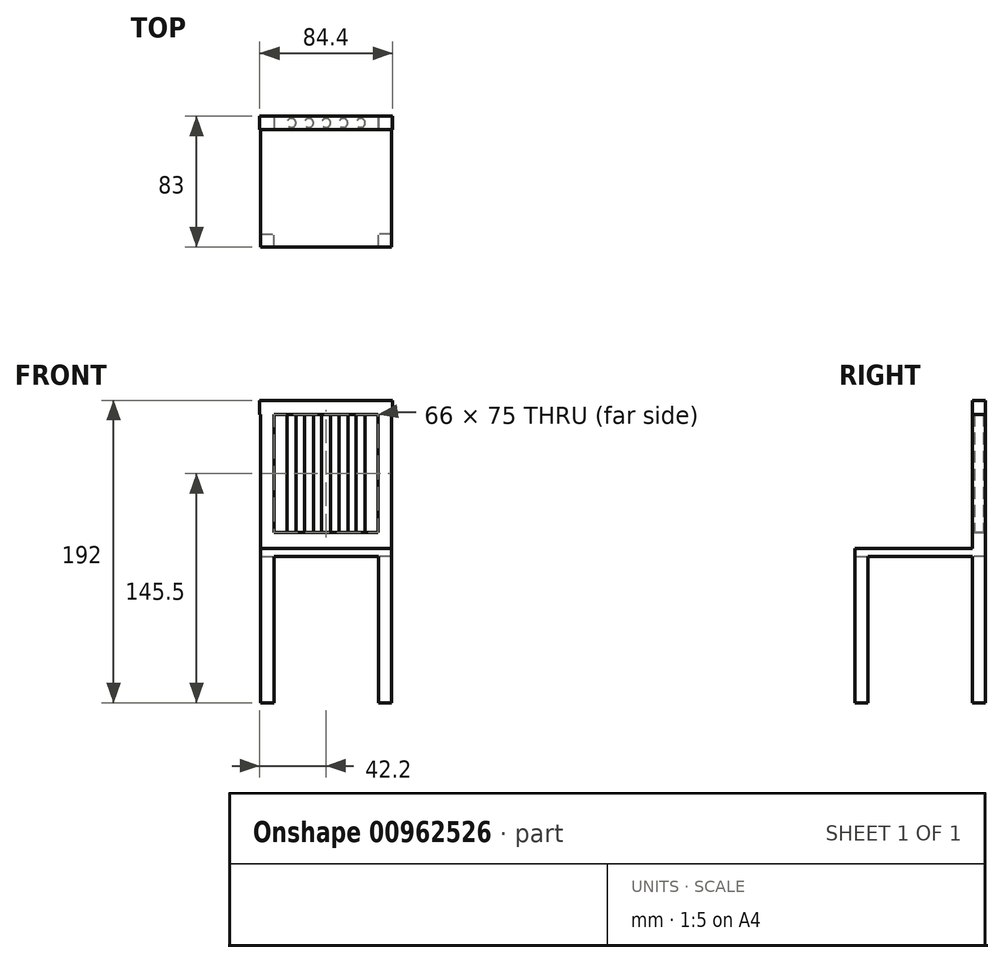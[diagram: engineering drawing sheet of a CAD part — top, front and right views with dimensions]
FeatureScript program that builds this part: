
annotation { "Feature Type Name" : "Feature", "Feature Type Description" : "" }
export const myFeature = defineFeature(function(context is Context, id is Id, definition is map)
    precondition{}
    {
        {
            var Q0;
            Q0=qCreatedBy(makeId("Top.planeOp"),FACE);
            var sketch = newSketch(context, id + "F0", { "sketchPlane" : qUnion([Q0])});
            skLineSegment(sketch, "E0.bottom", {"start": v(41.5, -41.5) * mm, "end": v(-41.5, -41.5) * mm});
            skLineSegment(sketch, "E0.top", {"start": v(41.5, 41.5) * mm, "end": v(-41.5, 41.5) * mm});
            skLineSegment(sketch, "E0.left", {"start": v(41.5, -41.5) * mm, "end": v(41.5, 41.5) * mm});
            skLineSegment(sketch, "E0.right", {"start": v(-41.5, -41.5) * mm, "end": v(-41.5, 41.5) * mm});
            skPoint(sketch, "E0.middle", {"position": v(0, 0) * mm});
            skSolve(sketch);
        }
        {
            var Q0;
            Q0 = qSketchRegion(id + "F0", true);
            extrude(context, id + "F1", {"entities" : qUnion([Q0]), "depth" : 5 * mm, "offsetDistance" : 25 * mm});
        }
        {
            var Q0;
            Q0=makeQuery(id+"F1.opExtrude","CAP_FACE",FACE,{"disambiguationData":[OSD([sQuery(id+"F0.wireOp",EDGE,"E0.bottom"),sQuery(id+"F0.wireOp",EDGE,"E0.top"),sQuery(id+"F0.wireOp",EDGE,"E0.left"),sQuery(id+"F0.wireOp",EDGE,"E0.right")])],"isStart":false});
            var sketch = newSketch(context, id + "F2", { "sketchPlane" : qUnion([Q0])});
            skLineSegment(sketch, "E1.bottom", {"start": v(-41.5, 41.5) * mm, "end": v(41.5, 41.5) * mm});
            skLineSegment(sketch, "E1.top", {"start": v(-41.5, 33) * mm, "end": v(41.5, 33) * mm});
            skLineSegment(sketch, "E1.left", {"start": v(-41.5, 41.5) * mm, "end": v(-41.5, 33) * mm});
            skLineSegment(sketch, "E1.right", {"start": v(41.5, 41.5) * mm, "end": v(41.5, 33) * mm});
            skSolve(sketch);
        }
        {
            var Q0;
            Q0 = qSketchRegion(id + "F2", true);
            extrude(context, id + "F3", {"entities" : qUnion([Q0]), "operationType" : NewBodyOperationType.ADD, "depth" : 10 * mm, "offsetDistance" : 25 * mm});
        }
        {
            var Q0;
            Q0=makeQuery(id+"F3.opExtrude","CAP_FACE",FACE,{"disambiguationData":[OSD([sQuery(id+"F2.wireOp",EDGE,"E1.bottom"),sQuery(id+"F2.wireOp",EDGE,"E1.top"),sQuery(id+"F2.wireOp",EDGE,"E1.left"),sQuery(id+"F2.wireOp",EDGE,"E1.right")])],"isStart":false});
            var sketch = newSketch(context, id + "F4", { "sketchPlane" : qUnion([Q0])});
            skLineSegment(sketch, "E2.bottom", {"start": v(-41.5, 41.5) * mm, "end": v(-33, 41.5) * mm});
            skLineSegment(sketch, "E2.top", {"start": v(-41.5, 33) * mm, "end": v(-33, 33) * mm});
            skLineSegment(sketch, "E2.left", {"start": v(-41.5, 41.5) * mm, "end": v(-41.5, 33) * mm});
            skLineSegment(sketch, "E2.right", {"start": v(-33, 41.5) * mm, "end": v(-33, 33) * mm});
            skLineSegment(sketch, "E3.MirrorCS", {"start": v(33, 41.5) * mm, "end": v(33, 33) * mm});
            skLineSegment(sketch, "E4.MirrorCS", {"start": v(41.5, 41.5) * mm, "end": v(41.5, 33) * mm});
            skLineSegment(sketch, "E5.MirrorCS", {"start": v(41.5, 41.5) * mm, "end": v(33, 41.5) * mm});
            skLineSegment(sketch, "E6.MirrorCS", {"start": v(41.5, 33) * mm, "end": v(33, 33) * mm});
            skSolve(sketch);
        }
        {
            var Q0;
            Q0 = qSketchRegion(id + "F4", true);
            extrude(context, id + "F5", {"entities" : qUnion([Q0]), "operationType" : NewBodyOperationType.ADD, "depth" : 75 * mm, "offsetDistance" : 25 * mm});
        }
        {
            var Q0;
            Q0=makeQuery(id+"F3.opExtrude","CAP_FACE",FACE,{"disambiguationData":[OSD([sQuery(id+"F2.wireOp",EDGE,"E1.bottom"),sQuery(id+"F2.wireOp",EDGE,"E1.top"),sQuery(id+"F2.wireOp",EDGE,"E1.left"),sQuery(id+"F2.wireOp",EDGE,"E1.right")])],"isStart":false});
            var sketch = newSketch(context, id + "F6", { "sketchPlane" : qUnion([Q0])});
            skCircle(sketch, "E7", {"center": v(-22, 37.25) * mm, "radius": 2.85 * mm});
            skPoint(sketch, "E7.centerSnap0", {"position": v(-33, 37.25) * mm});
            skCircle(sketch, "E8", {"center": v(-10.92, 37.25) * mm, "radius": 2.85 * mm});
            skCircle(sketch, "E9", {"center": v(0, 37.25) * mm, "radius": 2.85 * mm});
            skCircle(sketch, "E10.MirrorC", {"center": v(10.92, 37.25) * mm, "radius": 2.85 * mm});
            skCircle(sketch, "E11.MirrorC", {"center": v(22, 37.25) * mm, "radius": 2.85 * mm});
            skSolve(sketch);
        }
        {
            var Q0;
            Q0 = qSketchRegion(id + "F6", true);
            extrude(context, id + "F7", {"entities" : qUnion([Q0]), "operationType" : NewBodyOperationType.ADD, "depth" : 75 * mm, "offsetDistance" : 25 * mm});
        }
        {
            var Q0;
            Q0=makeQuery(id+"F7.opExtrude","CAP_FACE",FACE,{"disambiguationData":[OSD([sQuery(id+"F6.wireOp",EDGE,"E9")])],"isStart":false});
            var sketch = newSketch(context, id + "F8", { "sketchPlane" : qUnion([Q0])});
            skLineSegment(sketch, "E12.bottom", {"start": v(41.5, 33) * mm, "end": v(-41.5, 33) * mm});
            skLineSegment(sketch, "E12.top", {"start": v(41.5, 41.5) * mm, "end": v(-41.5, 41.5) * mm});
            skLineSegment(sketch, "E12.left", {"start": v(41.5, 33) * mm, "end": v(41.5, 41.5) * mm});
            skLineSegment(sketch, "E12.right", {"start": v(-41.5, 33) * mm, "end": v(-41.5, 41.5) * mm});
            skPoint(sketch, "E12.middle", {"position": v(0, 37.25) * mm});
            skLineSegment(sketch, "E13.bottom", {"start": v(-41.5, 41.5) * mm, "end": v(-42.2, 41.5) * mm});
            skLineSegment(sketch, "E13.top", {"start": v(-41.5, 33) * mm, "end": v(-42.2, 33) * mm});
            skLineSegment(sketch, "E13.left", {"start": v(-41.5, 41.5) * mm, "end": v(-41.5, 33) * mm});
            skLineSegment(sketch, "E13.right", {"start": v(-42.2, 41.5) * mm, "end": v(-42.2, 33) * mm});
            skLineSegment(sketch, "E14.MirrorCS", {"start": v(41.5, 33) * mm, "end": v(42.2, 33) * mm});
            skLineSegment(sketch, "E15.MirrorCS", {"start": v(42.2, 41.5) * mm, "end": v(42.2, 33) * mm});
            skLineSegment(sketch, "E16.MirrorCS", {"start": v(41.5, 41.5) * mm, "end": v(42.2, 41.5) * mm});
            skSolve(sketch);
        }
        {
            var Q0;
            Q0=makeQuery(id+"F8.imprint","IMPRINT",FACE,{"disambiguationData":[TD([[makeQuery(id+"F8.imprint","IMPRINT",EDGE,{"derivedFrom":sQuery(id+"F8.wireOp",EDGE,"E12.bottom")}),-1.0]])]});
            var Q1;
            Q1=makeQuery(id+"F8.imprint","IMPRINT",FACE,{"disambiguationData":[TD([[makeQuery(id+"F8.imprint","IMPRINT",EDGE,{"derivedFrom":makeQuery(id+"F7.opExtrude","CAP_EDGE",EDGE,{"disambiguationData":[OSD([sQuery(id+"F6.wireOp",EDGE,"E9")])],"isStart":false})}),1.0]])]});
            var Q2;
            Q2=makeQuery(id+"F8.imprint","IMPRINT",FACE,{"disambiguationData":[TD([[makeQuery(id+"F8.imprint","IMPRINT",EDGE,{"derivedFrom":sQuery(id+"F8.wireOp",EDGE,"E13.bottom")}),1.0]])]});
            var Q3;
            Q3=makeQuery(id+"F8.imprint","IMPRINT",FACE,{"disambiguationData":[TD([[makeQuery(id+"F8.imprint","IMPRINT",EDGE,{"derivedFrom":sQuery(id+"F8.wireOp",EDGE,"E12.left")}),-1.0]])]});
            extrude(context, id + "F9", {"entities" : qUnion([Q0, Q1, Q2, Q3]), "operationType" : NewBodyOperationType.ADD, "depth" : 9 * mm, "offsetDistance" : 25 * mm});
        }
        {
            var Q0;
            Q0=makeQuery(id+"F1.opExtrude","CAP_FACE",FACE,{"disambiguationData":[OSD([sQuery(id+"F0.wireOp",EDGE,"E0.bottom"),sQuery(id+"F0.wireOp",EDGE,"E0.top"),sQuery(id+"F0.wireOp",EDGE,"E0.left"),sQuery(id+"F0.wireOp",EDGE,"E0.right")])],"isStart":true});
            var sketch = newSketch(context, id + "F10", { "sketchPlane" : qUnion([Q0])});
            skLineSegment(sketch, "E17.bottom", {"start": v(-41.5, 41.5) * mm, "end": v(-33.2, 41.5) * mm});
            skLineSegment(sketch, "E17.top", {"start": v(-41.5, 33.2) * mm, "end": v(-33.2, 33.2) * mm});
            skLineSegment(sketch, "E17.left", {"start": v(-41.5, 41.5) * mm, "end": v(-41.5, 33.2) * mm});
            skLineSegment(sketch, "E17.right", {"start": v(-33.2, 41.5) * mm, "end": v(-33.2, 33.2) * mm});
            skLineSegment(sketch, "E18.MirrorCS", {"start": v(33.2, 41.5) * mm, "end": v(33.2, 33.2) * mm});
            skLineSegment(sketch, "E19.MirrorCS", {"start": v(41.5, 33.2) * mm, "end": v(33.2, 33.2) * mm});
            skLineSegment(sketch, "E20.MirrorCS", {"start": v(41.5, 41.5) * mm, "end": v(41.5, 33.2) * mm});
            skLineSegment(sketch, "E21.MirrorCS", {"start": v(41.5, 41.5) * mm, "end": v(33.2, 41.5) * mm});
            skLineSegment(sketch, "E22.MirrorCS", {"start": v(-41.5, -41.5) * mm, "end": v(-41.5, -33.2) * mm});
            skLineSegment(sketch, "E23.MirrorCS", {"start": v(-41.5, -41.5) * mm, "end": v(-33.2, -41.5) * mm});
            skLineSegment(sketch, "E24.MirrorCS", {"start": v(41.5, -41.5) * mm, "end": v(33.2, -41.5) * mm});
            skLineSegment(sketch, "E25.MirrorCS", {"start": v(-41.5, -33.2) * mm, "end": v(-33.2, -33.2) * mm});
            skLineSegment(sketch, "E26.MirrorCS", {"start": v(41.5, -41.5) * mm, "end": v(41.5, -33.2) * mm});
            skLineSegment(sketch, "E27.MirrorCS", {"start": v(41.5, -33.2) * mm, "end": v(33.2, -33.2) * mm});
            skLineSegment(sketch, "E28.MirrorCS", {"start": v(33.2, -41.5) * mm, "end": v(33.2, -33.2) * mm});
            skLineSegment(sketch, "E29.MirrorCS", {"start": v(-33.2, -41.5) * mm, "end": v(-33.2, -33.2) * mm});
            skSolve(sketch);
        }
        {
            var Q0;
            Q0 = qSketchRegion(id + "F10", true);
            extrude(context, id + "F11", {"entities" : qUnion([Q0]), "operationType" : NewBodyOperationType.ADD, "depth" : 93 * mm, "offsetDistance" : 25 * mm});
        }
    });
